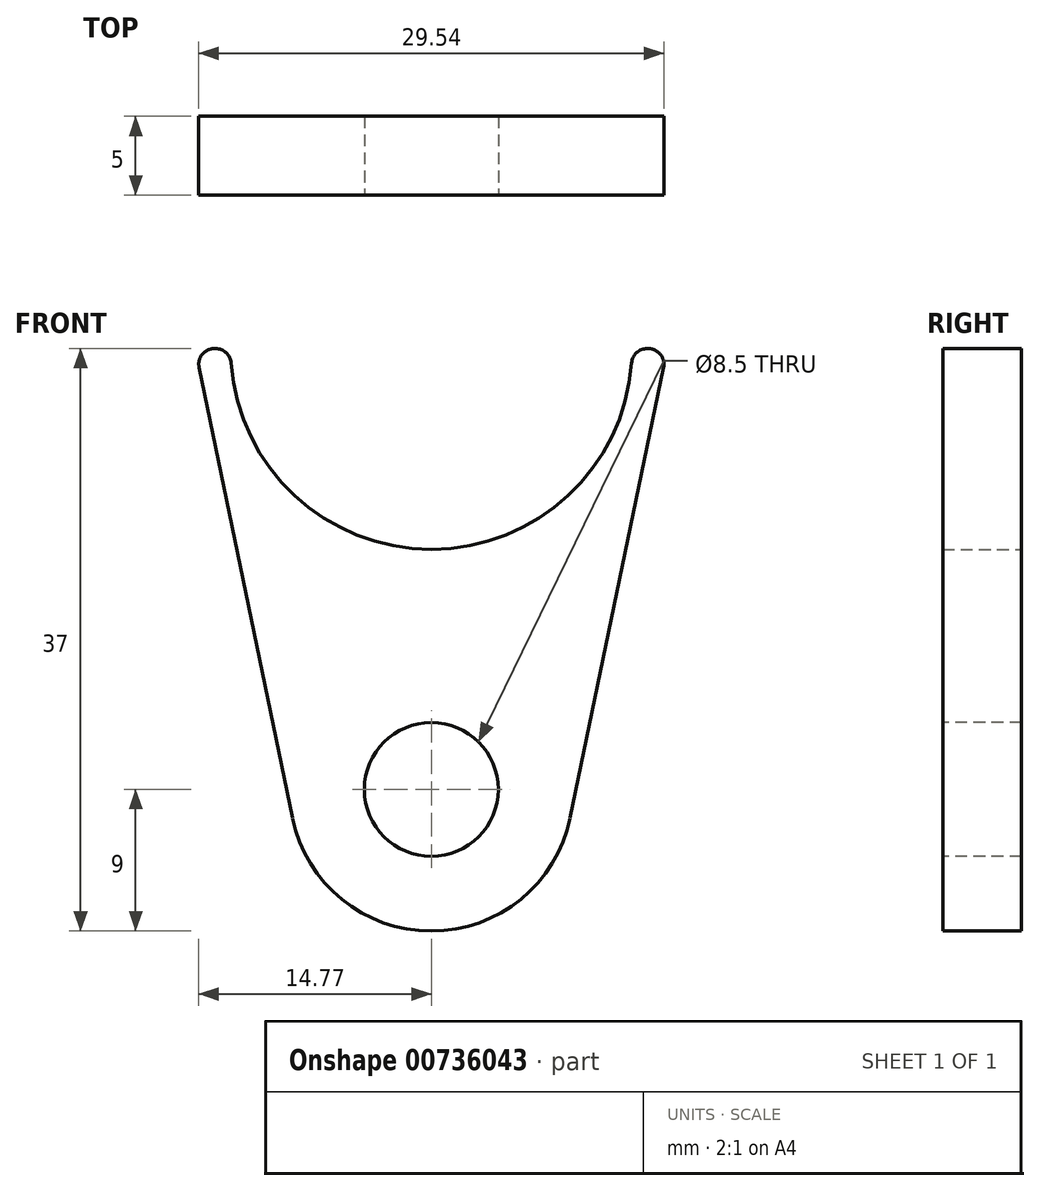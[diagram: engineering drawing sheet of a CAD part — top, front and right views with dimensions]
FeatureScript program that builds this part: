
annotation { "Feature Type Name" : "Feature", "Feature Type Description" : "" }
export const myFeature = defineFeature(function(context is Context, id is Id, definition is map)
    precondition{}
    {
        {
            var Q0;
            Q0=qCreatedBy(makeId("Front.planeOp"),FACE);
            var sketch = newSketch(context, id + "F0", { "sketchPlane" : qUnion([Q0])});
            skLineSegment(sketch, "E0", {"start": v(15, 0) * mm, "end": v(15, 0) * mm});
            skArc(sketch, "E1", {"start": v(-8.81, -29.83) * mm, "mid": v(0, -37) * mm, "end": v(8.81, -29.83) * mm});
            skLineSegment(sketch, "E2", {"start": v(-15, 0) * mm, "end": v(-8.81, -29.83) * mm});
            skLineSegment(sketch, "E3", {"start": v(15, 0) * mm, "end": v(8.81, -29.83) * mm});
            skArc(sketch, "E4", {"start": v(-12.75, 0) * mm, "mid": v(0, -12.75) * mm, "end": v(12.75, 0) * mm});
            skLineSegment(sketch, "E5", {"start": v(-12.75, 0) * mm, "end": v(-15, 0) * mm});
            skLineSegment(sketch, "E6", {"start": v(12.75, 0) * mm, "end": v(15, 0) * mm});
            skLineSegment(sketch, "E7.trimOffspring", {"start": v(-15, 0) * mm, "end": v(-15, 0) * mm});
            skSolve(sketch);
        }
        {
            var Q0;
            Q0=makeQuery(id+"F0.imprint","IMPRINT",FACE,{"disambiguationData":[TD([[makeQuery(id+"F0.imprint","IMPRINT",EDGE,{"derivedFrom":sQuery(id+"F0.wireOp",EDGE,"E1")}),1.0]])]});
            extrude(context, id + "F1", {"entities" : qUnion([Q0]), "depth" : 5 * mm, "offsetDistance" : 25 * mm});
        }
        {
            var Q0;
            Q0=makeQuery(id+"F1.opExtrude","CAP_FACE",FACE,{"disambiguationData":[OSD([sQuery(id+"F0.wireOp",EDGE,"E1"),sQuery(id+"F0.wireOp",EDGE,"E2"),sQuery(id+"F0.wireOp",EDGE,"E3"),sQuery(id+"F0.wireOp",EDGE,"E4"),sQuery(id+"F0.wireOp",EDGE,"E5"),sQuery(id+"F0.wireOp",EDGE,"E6")])],"isStart":false});
            var sketch = newSketch(context, id + "F2", { "sketchPlane" : qUnion([Q0])});
            skPoint(sketch, "E8", {"position": v(0, -28) * mm});
            skSolve(sketch);
        }
        {
            var Q0;
            Q0=sQuery(id+"F2.wireOp",VERTEX,"E8");
            var Q1;
            Q1=makeQuery(id+"F1.opExtrude","SWEPT_BODY",BODY,{"disambiguationData":[OSD([sQuery(id+"F0.wireOp",EDGE,"E1"),sQuery(id+"F0.wireOp",EDGE,"E2"),sQuery(id+"F0.wireOp",EDGE,"E3"),sQuery(id+"F0.wireOp",EDGE,"E4"),sQuery(id+"F0.wireOp",EDGE,"E5"),sQuery(id+"F0.wireOp",EDGE,"E6")])]});
            hole(context, id + "F3", {"style" : HoleStyle.SIMPLE, "endStyle" : HoleEndStyle.THROUGH, "holeDiameter" : 8.5 * mm, "majorDiameter" : 6 * mm, "tappedDepth" : 12 * mm, "tapClearance" : 3, "startFromSketch" : true, "locations" : qUnion([Q0]), "scope" : qUnion([Q1])});
        }
        {
            var Q0;
            Q0=makeQuery(id+"F1.opExtrude","SWEPT_EDGE",EDGE,{"disambiguationData":[OSD([sQuery(id+"F0.wireOp",EDGE,"E3"),sQuery(id+"F0.wireOp",EDGE,"E6")])]});
            var Q1;
            Q1=makeQuery(id+"F1.opExtrude","SWEPT_EDGE",EDGE,{"disambiguationData":[OSD([sQuery(id+"F0.wireOp",EDGE,"E2"),sQuery(id+"F0.wireOp",EDGE,"E5")])]});
            var Q2;
            Q2=makeQuery(id+"F1.opExtrude","SWEPT_EDGE",EDGE,{"disambiguationData":[OSD([sQuery(id+"F0.wireOp",EDGE,"E4"),sQuery(id+"F0.wireOp",EDGE,"E5")])]});
            var Q3;
            Q3=makeQuery(id+"F1.opExtrude","SWEPT_EDGE",EDGE,{"disambiguationData":[OSD([sQuery(id+"F0.wireOp",EDGE,"E4"),sQuery(id+"F0.wireOp",EDGE,"E6")])]});
            fillet(context, id + "F4", {"entities" : qUnion([Q0, Q1, Q2, Q3]), "radius" : 1 * mm, "tangentPropagation" : true, "allowEdgeOverflow" : false});
        }
    });
